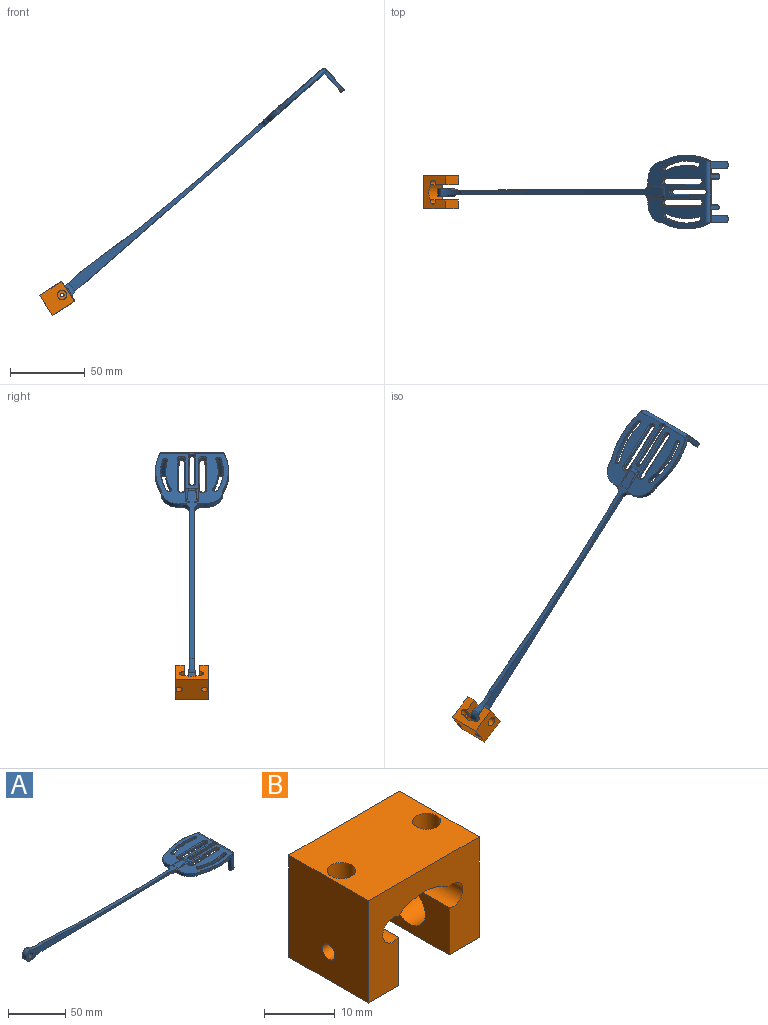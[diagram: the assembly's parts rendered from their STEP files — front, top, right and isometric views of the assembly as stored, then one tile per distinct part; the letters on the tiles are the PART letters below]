
ASSEMBLY  parts=2 mates=1
PART A: 187 faces, bbox 240.3x58.3x26.7 mm
  f0: plane 4.82x2.08mm, normal (-0.02,0,1), area 1.8mm2, adj f2,f5,f6,f8,f107,f164
  f1: plane 14.7x2.58mm, normal (0,1,0), area 33.5mm2, adj f3,f6,f9,f12
  f2: plane 14.7x2.58mm, normal (0,-1,0), area 33.5mm2, adj f0,f3,f8,f11,f12
  f3: cylinder r=2.41mm len=4.82mm, axis (1,0,0.02), area 17.3mm2, adj f1,f2,f7,f10
  f4: plane 16.81x4.31mm, normal (-1,0,-0.02), area 70.5mm2, adj f9,f10,f11,f12
  f5: plane 16.81x4.31mm, normal (1,0,0.02), area 70.5mm2, adj f0,f6,f7,f8
  f6: cylinder r=0.25mm len=14.66mm, axis (-0.02,0,1), area 5.8mm2, adj f0,f1,f5,f7
  f7: torus R=2.16mm, axis (1,0,0.02), area 2.9mm2, adj f3,f5,f6,f8
  f8: cylinder r=0.25mm len=14.66mm, axis (0.02,0,-1), area 5.8mm2, adj f0,f2,f5,f7
  f9: cylinder r=0.25mm len=14.66mm, axis (0.02,0,-1), area 5.8mm2, adj f1,f4,f10,f12
  f10: torus R=2.16mm, axis (1,0,0.02), area 2.9mm2, adj f3,f4,f9,f11
  f11: cylinder r=0.25mm len=14.66mm, axis (-0.02,0,1), area 5.8mm2, adj f2,f4,f10,f12
  f12: plane 215.52x47.88mm, normal (0.02,0,-1), area 1943.7mm2, adj f1,f2,f4,f9,f11,f15,f65,f66
  f13: plane 40.81x17.58mm, normal (1,0,0.02), area 137.9mm2, adj f60,f91,f92,f93,f94,f95,f96,f97
  f14: plane 166.07x7.87mm, normal (0,1,0), area 618.5mm2, adj f15,f16,f23,f58,f116,f119
  f15: cylinder r=49.31mm len=16.98mm, axis (0,1,0), area 63.7mm2, adj f12,f14,f18,f19,f20,f21,f22,f23
  f16: cylinder r=25.53mm len=16.98mm, axis (0,1,0), area 64.7mm2, adj f14,f18,f19,f20,f21,f22,f23,f24
  f17: cylinder r=3.17mm len=6.35mm, axis (0,1,0), area 101.3mm2, adj f19,f20
  f18: cylinder r=5.72mm len=11.44mm, axis (0,1,0), area 91.3mm2, adj f15,f16,f19,f20
  f19: plane 11.44x11.44mm, normal (0,-1,0), area 69.3mm2, adj f15,f16,f17,f18,f22
  f20: plane 11.44x11.44mm, normal (0,1,0), area 69.3mm2, adj f15,f16,f17,f18,f23
  f21: plane 166.07x7.87mm, normal (0,-1,0), area 618.5mm2, adj f15,f16,f22,f59,f111,f112
  f22: torus R=8.77mm, axis (0,-1,0), area 31.3mm2, adj f15,f16,f19,f21
  f23: torus R=8.77mm, axis (0,-1,0), area 31.3mm2, adj f14,f15,f16,f20
  f24: cylinder r=1259.21mm len=175.32mm, axis (0,1,0), area 578.9mm2, adj f16,f25,f26,f45,f46,f47,f57,f110
  f25: plane 0.48x0.03mm, normal (0,1,0), area 0mm2, adj f24,f26,f124
  f26: plane 51.29x48.86mm, normal (-0.02,0,1), area 1354.2mm2, adj f24,f25,f43,f44,f46,f47,f48,f55
  f27: cylinder r=1.91mm len=3.81mm, axis (0.02,0,-1), area 10.8mm2, adj f28,f54,f142,f152
  f28: plane 31.36x2.4mm, normal (0,-1,0), area 55.7mm2, adj f27,f140,f153,f155
  f29: cylinder r=1.91mm len=3.81mm, axis (0.02,0,-1), area 10.8mm2, adj f139,f147,f149,f155
  f30: plane 31.4x2.4mm, normal (0,-1,0), area 55.8mm2, adj f31,f50,f134,f143
  f31: cylinder r=1.91mm len=3.81mm, axis (0.02,0,-1), area 10.9mm2, adj f30,f32,f132,f144
  f32: plane 31.55x2.4mm, normal (0,1,0), area 56mm2, adj f31,f50,f131,f146
  f33: plane 29.04x2.35mm, normal (0,-1,0), area 51.6mm2, adj f34,f51,f128,f137
  f34: cylinder r=1.52mm len=3.05mm, axis (0.02,0,-1), area 8.5mm2, adj f33,f35,f126,f138
  f35: plane 29.04x2.35mm, normal (0,1,0), area 51.6mm2, adj f34,f51,f125,f136
  f36: cylinder r=46.75mm len=30.39mm, axis (0.02,0,-1), area 78.7mm2, adj f37,f52,f167,f175
  f37: cylinder r=1.52mm len=2.93mm, axis (0.02,0,-1), area 12.2mm2, adj f36,f38,f166,f174
  f38: cylinder r=49.8mm len=31.72mm, axis (0.02,0,-1), area 82.1mm2, adj f37,f52,f168,f176
  f39: cylinder r=1.6mm len=3.19mm, axis (0.02,0,-1), area 13.8mm2, adj f40,f53,f172,f180
  f40: cylinder r=49.8mm len=29.79mm, axis (0.02,0,-1), area 77mm2, adj f39,f41,f170,f178
  f41: cylinder r=1.53mm len=2.97mm, axis (0.02,0,-1), area 12.7mm2, adj f40,f53,f171,f179
  f42: cylinder r=53.61mm len=41.04mm, axis (0.02,0,-1), area 93.4mm2, adj f43,f108,f109,f164
  f43: plane 3.08x0.98mm, normal (0,-1,0), area 0.6mm2, adj f26,f42,f44,f109,f164,f186
  f44: plane 3.35x2.86mm, normal (-0.1,-0.99,0), area 9mm2, adj f26,f43,f45,f114,f124,f186
  f45: cylinder r=12.67mm len=15.14mm, axis (0.02,0,-1), area 57.3mm2, adj f24,f44,f59,f110,f114,f124
  f46: plane 0.51x0.03mm, normal (0,-1,0), area 0mm2, adj f24,f26,f47
  f47: cylinder r=12.67mm len=19.05mm, axis (0.02,0,-1), area 64.5mm2, adj f24,f26,f46,f58,f115,f117,f182,f185
  f48: plane 3.1x2.02mm, normal (0,1,0), area 3.6mm2, adj f26,f49,f89,f160,f183,f185
  f49: cylinder r=53.61mm len=41.06mm, axis (0.02,0,-1), area 95.4mm2, adj f48,f89,f90,f91,f160,f161,f162
  f50: cylinder r=1.91mm len=3.81mm, axis (0.02,0,-1), area 10.6mm2, adj f30,f32,f133,f145
  f51: cylinder r=1.52mm len=3.05mm, axis (0.02,0,-1), area 8.5mm2, adj f33,f35,f127,f129,f130,f135
  f52: cylinder r=1.62mm len=3.11mm, axis (0.02,0,-1), area 10.7mm2, adj f36,f38,f169,f177
  f53: cylinder r=46.75mm len=28.78mm, axis (0.02,0,-1), area 74.4mm2, adj f39,f41,f173,f181
  f54: plane 31.48x2.4mm, normal (0,1,0), area 55.9mm2, adj f27,f141,f149,f151
  f55: cylinder r=2.54mm len=13.62mm, axis (1,0,0.02), area 11.9mm2, adj f26,f120,f121
  f56: cylinder r=2.54mm len=13.62mm, axis (-1,0,-0.02), area 11.9mm2, adj f26,f122,f123
  f57: cylinder r=5.08mm len=7.61mm, axis (0,1,0), area 16mm2, adj f24,f26,f121,f123
  f58: cylinder r=5.08mm len=5.47mm, axis (0.02,0,-1), area 25.7mm2, adj f14,f47,f115,f118
  f59: cylinder r=5.08mm len=5.47mm, axis (0.02,0,-1), area 25.7mm2, adj f21,f45,f110,f113
  f60: cylinder r=2.54mm len=42.57mm, axis (0,1,0), area 163.4mm2, adj f13,f26,f90,f108,f129
  f61: plane 5.92x2.4mm, normal (0,1,0), area 13.4mm2, adj f63,f78,f80,f103
  f62: plane 5.92x2.4mm, normal (0,-1,0), area 13.4mm2, adj f63,f73,f74,f105
  f63: cylinder r=1.71mm len=3.41mm, axis (1,0,0.02), area 12.3mm2, adj f61,f62,f76,f104
  f64: plane 7.32x2.9mm, normal (-1,0,-0.02), area 20.4mm2, adj f74,f76,f77,f78
  f65: plane 6.17x2.28mm, normal (0,1,0), area 13.2mm2, adj f12,f67,f98,f157
  f66: plane 6.17x2.28mm, normal (0,-1,0), area 13.2mm2, adj f12,f67,f100,f159
  f67: cylinder r=1.77mm len=3.55mm, axis (1,0,0.02), area 14.1mm2, adj f65,f66,f99,f158
  f68: plane 8x2.78mm, normal (-1,0,-0.02), area 20.6mm2, adj f12,f157,f158,f159
  f69: plane 14.45x2.57mm, normal (0,1,0), area 32.9mm2, adj f71,f81,f82,f93
  f70: plane 14.45x2.57mm, normal (0,-1,0), area 32.9mm2, adj f71,f85,f88,f95
  f71: cylinder r=2.41mm len=4.82mm, axis (1,0,0.02), area 17.3mm2, adj f69,f70,f83,f94
  f72: plane 16.56x4.31mm, normal (-1,0,-0.02), area 69.4mm2, adj f81,f83,f85,f86
  f73: cylinder r=0.25mm len=2.29mm, axis (1,0,0.02), area 0.9mm2, adj f12,f62,f75,f106
  f74: cylinder r=0.25mm len=5.88mm, axis (-0.02,0,1), area 2.3mm2, adj f62,f64,f75,f76
  f75: torus R=0.51mm, axis (-0.02,0,1), area 0.2mm2, adj f12,f73,f74,f77
  f76: torus R=1.45mm, axis (1,0,0.02), area 2mm2, adj f63,f64,f74,f78
  f77: cylinder r=0.25mm len=2.9mm, axis (0,1,0), area 1.2mm2, adj f12,f64,f75,f79
  f78: cylinder r=0.25mm len=5.88mm, axis (0.02,0,-1), area 2.3mm2, adj f61,f64,f76,f79
  f79: torus R=0.51mm, axis (-0.02,0,1), area 0.2mm2, adj f12,f77,f78,f80
  f80: cylinder r=0.25mm len=2.29mm, axis (-1,0,-0.02), area 0.9mm2, adj f12,f61,f79,f102
  f81: cylinder r=0.25mm len=14.41mm, axis (0.02,0,-1), area 5.7mm2, adj f69,f72,f83,f84
  f82: cylinder r=0.25mm len=2.29mm, axis (-1,0,-0.02), area 0.6mm2, adj f69,f84,f92,f162
  f83: torus R=2.15mm, axis (1,0,0.02), area 2.9mm2, adj f71,f72,f81,f85
  f84: torus R=0.51mm, axis (-0.02,0,1), area 0.2mm2, adj f12,f81,f82,f86,f161
  f85: cylinder r=0.25mm len=14.41mm, axis (-0.02,0,1), area 5.7mm2, adj f70,f72,f83,f87
  f86: cylinder r=0.25mm len=4.31mm, axis (0,-1,0), area 1.7mm2, adj f12,f72,f84,f87
  f87: torus R=0.51mm, axis (-0.02,0,1), area 0.2mm2, adj f12,f85,f86,f88
  f88: cylinder r=0.25mm len=2.29mm, axis (-1,0,-0.02), area 0.9mm2, adj f12,f70,f87,f96
  f89: torus R=53.35mm, axis (0.02,0,-1), area 15.7mm2, adj f26,f48,f49,f90
  f90: bspline ~3.18x3.03mm, area 1.3mm2, adj f49,f60,f89,f91
  f91: cylinder r=0.25mm len=0.54mm, axis (0.02,0,-1), area 0.2mm2, adj f13,f49,f90,f163
  f92: torus R=0.51mm, axis (1,0,0.02), area 0mm2, adj f13,f82,f93,f163
  f93: cylinder r=0.25mm len=14.41mm, axis (-0.02,0,1), area 5.7mm2, adj f13,f69,f92,f94
  f94: torus R=2.15mm, axis (1,0,0.02), area 2.9mm2, adj f13,f71,f93,f95
  f95: cylinder r=0.25mm len=14.41mm, axis (0.02,0,-1), area 5.7mm2, adj f13,f70,f94,f96
  f96: torus R=0.51mm, axis (1,0,0.02), area 0.2mm2, adj f13,f88,f95,f97
  f97: cylinder r=0.25mm len=3.69mm, axis (0,1,0), area 1.4mm2, adj f12,f13,f96,f98
  f98: cylinder r=0.25mm len=6.42mm, axis (-0.02,0,1), area 2.5mm2, adj f13,f65,f97,f99
  f99: torus R=1.52mm, axis (1,0,0.02), area 2.5mm2, adj f13,f67,f98,f100
  f100: cylinder r=0.25mm len=6.42mm, axis (0.02,0,-1), area 2.5mm2, adj f13,f66,f99,f101
  f101: cylinder r=0.25mm len=17.3mm, axis (0,1,0), area 6.8mm2, adj f12,f13,f100,f102
  f102: torus R=0.51mm, axis (1,0,0.02), area 0.2mm2, adj f13,f80,f101,f103
  f103: cylinder r=0.25mm len=5.88mm, axis (-0.02,0,1), area 2.3mm2, adj f13,f61,f102,f104
  f104: torus R=1.45mm, axis (1,0,0.02), area 2mm2, adj f13,f63,f103,f105
  f105: cylinder r=0.25mm len=5.88mm, axis (0.02,0,-1), area 2.3mm2, adj f13,f62,f104,f106
  f106: torus R=0.51mm, axis (1,0,0.02), area 0.2mm2, adj f13,f73,f105,f107
  f107: cylinder r=0.25mm len=7.54mm, axis (0,1,0), area 3mm2, adj f0,f12,f13,f106,f165
  f108: bspline ~3.18x3.03mm, area 1.3mm2, adj f42,f60,f109,f165
  f109: torus R=53.35mm, axis (0.02,0,-1), area 15.7mm2, adj f26,f42,f43,f108
  f110: bspline ~6.25x5.99mm, area 0.3mm2, adj f24,f45,f59,f111
  f111: torus R=1259.23mm, axis (0,-1,0), area 6mm2, adj f16,f21,f24,f110
  f112: cylinder r=0.02mm len=157.3mm, axis (-1,0,-0.02), area 6mm2, adj f12,f15,f21,f113
  f113: torus R=5.1mm, axis (-0.02,0,1), area 0.3mm2, adj f12,f59,f112,f114
  f114: torus R=12.65mm, axis (-0.02,0,1), area 0.7mm2, adj f12,f44,f45,f113,f186
  f115: bspline ~6.25x5.99mm, area 0.3mm2, adj f24,f47,f58,f116
  f116: torus R=1259.23mm, axis (0,-1,0), area 6mm2, adj f14,f16,f24,f115
  f117: torus R=12.65mm, axis (-0.02,0,1), area 0.7mm2, adj f12,f47,f118,f182
  f118: torus R=5.1mm, axis (-0.02,0,1), area 0.3mm2, adj f12,f58,f117,f119
  f119: cylinder r=0.02mm len=157.3mm, axis (1,0,0.02), area 6mm2, adj f12,f14,f15,f118
  f120: bspline ~14.73x1.79mm, area 0.6mm2, adj f24,f26,f55,f121
  f121: bspline ~3.04x1.65mm, area 0.2mm2, adj f26,f55,f57,f120
  f122: bspline ~12.08x1.62mm, area 0.6mm2, adj f24,f26,f56,f123
  f123: bspline ~3.04x1.65mm, area 0.2mm2, adj f26,f56,f57,f122
  f124: torus R=12.6mm, axis (0.02,0,-1), area 2.7mm2, adj f24,f25,f26,f44,f45
  f125: cylinder r=0.76mm len=29.02mm, axis (-1,0,-0.02), area 34.7mm2, adj f26,f35,f126,f127
  f126: torus R=2.29mm, axis (0.02,0,-1), area 6.8mm2, adj f26,f34,f125,f128
  f127: torus R=2.29mm, axis (0.02,0,-1), area 1.5mm2, adj f26,f51,f125,f129
  f128: cylinder r=0.76mm len=29.03mm, axis (1,0,0.02), area 34.7mm2, adj f26,f33,f126,f130
  f129: bspline ~3.93x1.95mm, area 4.7mm2, adj f51,f60,f127,f130
  f130: torus R=2.29mm, axis (0.02,0,-1), area 1.5mm2, adj f26,f51,f128,f129
  f131: cylinder r=0.76mm len=31.53mm, axis (-1,0,-0.02), area 37.7mm2, adj f12,f32,f132,f133
  f132: torus R=2.67mm, axis (-0.02,0,1), area 8.4mm2, adj f12,f31,f131,f134
  f133: torus R=2.67mm, axis (-0.02,0,1), area 8.2mm2, adj f12,f50,f131,f134
  f134: cylinder r=0.76mm len=31.38mm, axis (1,0,0.02), area 37.5mm2, adj f12,f30,f132,f133
  f135: torus R=2.29mm, axis (-0.02,0,1), area 6.8mm2, adj f12,f51,f136,f137
  f136: cylinder r=0.76mm len=29.02mm, axis (-1,0,-0.02), area 34.7mm2, adj f12,f35,f135,f138
  f137: cylinder r=0.76mm len=29.03mm, axis (1,0,0.02), area 34.7mm2, adj f12,f33,f135,f138
  f138: torus R=2.29mm, axis (-0.02,0,1), area 6.8mm2, adj f12,f34,f136,f137
  f139: torus R=2.67mm, axis (-0.02,0,1), area 8.4mm2, adj f12,f29,f148,f156
  f140: cylinder r=0.76mm len=31.34mm, axis (1,0,0.02), area 37.5mm2, adj f12,f28,f142,f156
  f141: cylinder r=0.76mm len=31.46mm, axis (-1,0,-0.02), area 37.6mm2, adj f12,f54,f142,f148
  f142: torus R=2.67mm, axis (-0.02,0,1), area 8.3mm2, adj f12,f27,f140,f141
  f143: cylinder r=0.76mm len=31.38mm, axis (1,0,0.02), area 37.5mm2, adj f26,f30,f144,f145
  f144: torus R=2.67mm, axis (0.02,0,-1), area 8.4mm2, adj f26,f31,f143,f146
  f145: torus R=2.67mm, axis (0.02,0,-1), area 8.2mm2, adj f26,f50,f143,f146
  f146: cylinder r=0.76mm len=31.53mm, axis (-1,0,-0.02), area 37.7mm2, adj f26,f32,f144,f145
  f147: torus R=2.67mm, axis (0.02,0,-1), area 8.4mm2, adj f26,f29,f150,f154
  f148: sphere r=0.76mm, area 0mm2, adj f139,f141,f149
  f149: cylinder r=0.76mm len=1.78mm, axis (0.02,0,-1), area 0mm2, adj f29,f54,f148,f150
  f150: sphere r=0.76mm, area 0mm2, adj f147,f149,f151
  f151: cylinder r=0.76mm len=31.46mm, axis (-1,0,-0.02), area 37.6mm2, adj f26,f54,f150,f152
  f152: torus R=2.67mm, axis (0.02,0,-1), area 8.3mm2, adj f26,f27,f151,f153
  f153: cylinder r=0.76mm len=31.34mm, axis (1,0,0.02), area 37.5mm2, adj f26,f28,f152,f154
  f154: sphere r=0.76mm, area 0mm2, adj f147,f153,f155
  f155: cylinder r=0.76mm len=1.78mm, axis (0.02,0,-1), area 0mm2, adj f28,f29,f154,f156
  f156: sphere r=0.76mm, area 0mm2, adj f139,f140,f155
  f157: cylinder r=0.38mm len=6.19mm, axis (0.02,0,-1), area 3.7mm2, adj f12,f65,f68,f158
  f158: torus R=1.39mm, axis (1,0,0.02), area 3.6mm2, adj f67,f68,f157,f159
  f159: cylinder r=0.38mm len=6.19mm, axis (-0.02,0,1), area 3.7mm2, adj f12,f66,f68,f158
  f160: torus R=52.85mm, axis (-0.02,0,1), area 46.7mm2, adj f12,f48,f49,f161,f183
  f161: bspline ~0.79x0.77mm, area 0.2mm2, adj f49,f84,f160,f162
  f162: bspline ~2.9x1.03mm, area 1.9mm2, adj f49,f82,f161,f163
  f163: bspline ~0.56x0.32mm, area 0.1mm2, adj f13,f91,f92,f162
  f164: torus R=52.85mm, axis (-0.02,0,1), area 49.7mm2, adj f0,f12,f42,f43,f165,f186
  f165: bspline ~0.93x0.87mm, area 0.4mm2, adj f13,f107,f108,f164
  f166: torus R=2.03mm, axis (-0.02,0,1), area 4.3mm2, adj f12,f37,f167,f168
  f167: torus R=46.24mm, axis (-0.02,0,1), area 24.7mm2, adj f12,f36,f166,f169
  f168: torus R=50.31mm, axis (-0.02,0,1), area 25.9mm2, adj f12,f38,f166,f169
  f169: torus R=2.12mm, axis (-0.02,0,1), area 3.8mm2, adj f12,f52,f167,f168
  f170: torus R=50.31mm, axis (-0.02,0,1), area 24.2mm2, adj f12,f40,f171,f172
  f171: torus R=2.03mm, axis (-0.02,0,1), area 4.4mm2, adj f12,f41,f170,f173
  f172: torus R=2.1mm, axis (-0.02,0,1), area 4.8mm2, adj f12,f39,f170,f173
  f173: torus R=46.24mm, axis (-0.02,0,1), area 23.3mm2, adj f12,f53,f171,f172
  f174: torus R=1.78mm, axis (0.02,0,-1), area 2mm2, adj f26,f37,f175,f176
  f175: torus R=46.5mm, axis (0.02,0,-1), area 12.3mm2, adj f26,f36,f174,f177
  f176: torus R=50.05mm, axis (0.02,0,-1), area 12.9mm2, adj f26,f38,f174,f177
  f177: torus R=1.87mm, axis (0.02,0,-1), area 1.8mm2, adj f26,f52,f175,f176
  f178: torus R=50.05mm, axis (0.02,0,-1), area 12.1mm2, adj f26,f40,f179,f180
  f179: torus R=1.78mm, axis (0.02,0,-1), area 2.1mm2, adj f26,f41,f178,f181
  f180: torus R=1.85mm, axis (0.02,0,-1), area 2.3mm2, adj f26,f39,f178,f181
  f181: torus R=46.5mm, axis (0.02,0,-1), area 11.7mm2, adj f26,f53,f179,f180
  f182: bspline ~2.45x0.52mm, area 0mm2, adj f47,f117,f183,f184
  f183: cylinder r=0.38mm len=4.31mm, axis (-1,0,-0.02), area 1.6mm2, adj f12,f48,f160,f182,f184
  f184: bspline ~0.05x0.05mm, area 0mm2, adj f182,f183,f185
  f185: cylinder r=0.38mm len=2.96mm, axis (0.02,0,-1), area 0.1mm2, adj f26,f47,f48,f184
  f186: cylinder r=0.38mm len=4.31mm, axis (1,0,0.02), area 1.3mm2, adj f12,f43,f44,f114,f164
PART B: 18 faces, bbox 22.2x15.9x17.7 mm
  f0: cylinder r=2.1mm len=15.88mm, axis (0,1,0), area 122mm2, adj f4,f5,f11,f12,f16,f17
  f1: cylinder r=2mm len=15.88mm, axis (0,1,0), area 111.4mm2, adj f5,f6,f11,f12,f14,f15
  f2: cylinder r=3.17mm len=6.35mm, axis (1,0,0), area 119.1mm2, adj f6,f8,f15
  f3: plane 15.88x6.01mm, normal (0,0,-1), area 95.4mm2, adj f4,f10,f11,f12
  f4: plane 15.89x8.38mm, normal (1,0,0), area 127.8mm2, adj f0,f3,f11,f12,f13
  f5: cylinder r=8.81mm len=15.88mm, axis (0,1,0), area 171.9mm2, adj f0,f1,f11,f12
  f6: plane 15.88x8.09mm, normal (-1,0,0), area 96.8mm2, adj f1,f2,f7,f11,f12
  f7: plane 15.88x6.01mm, normal (0,0,-1), area 95.4mm2, adj f6,f8,f11,f12
  f8: plane 17.4x15.88mm, normal (1,0,0), area 244.5mm2, adj f2,f7,f9,f11,f12
  f9: plane 22.14x15.88mm, normal (0,0,1), area 326.9mm2, adj f8,f10,f11,f12,f14,f16
  f10: plane 17.68x15.88mm, normal (-1,0,0), area 275.6mm2, adj f3,f9,f11,f12,f13
  f11: plane 22.14x17.68mm, normal (0,-1,0), area 236.1mm2, adj f0,f1,f3,f4,f5,f6,f7,f8
  f12: plane 22.14x17.68mm, normal (0,1,0), area 236.1mm2, adj f0,f1,f3,f4,f5,f6,f7,f8
  f13: cylinder r=1.27mm len=6mm, axis (1,0,0), area 47.9mm2, adj f4,f10
  f14: cylinder r=1.98mm len=8.73mm, axis (0,0,1), area 95.5mm2, adj f1,f9,f15
  f15: cone r=0mm half-angle=59deg, axis (0,0,1), area 12.2mm2, adj f1,f2,f14
  f16: cylinder r=1.98mm len=8.73mm, axis (0,0,1), area 92.7mm2, adj f0,f9,f17
  f17: cone r=0mm half-angle=59deg, axis (0,0,1), area 11.9mm2, adj f0,f16
PLACE A rot(axis=(0,-1,0),40deg) t=(90.66,100.67,8.24)mm
PLACE B rot(axis=(0.66,-0.66,-0.36),140.8deg) t=(90.67,100.66,8.24)mm
MATE revolute B.f6 <-> A.f17  axis (0,1,0) through (90.66,95.59,8.24)mm
